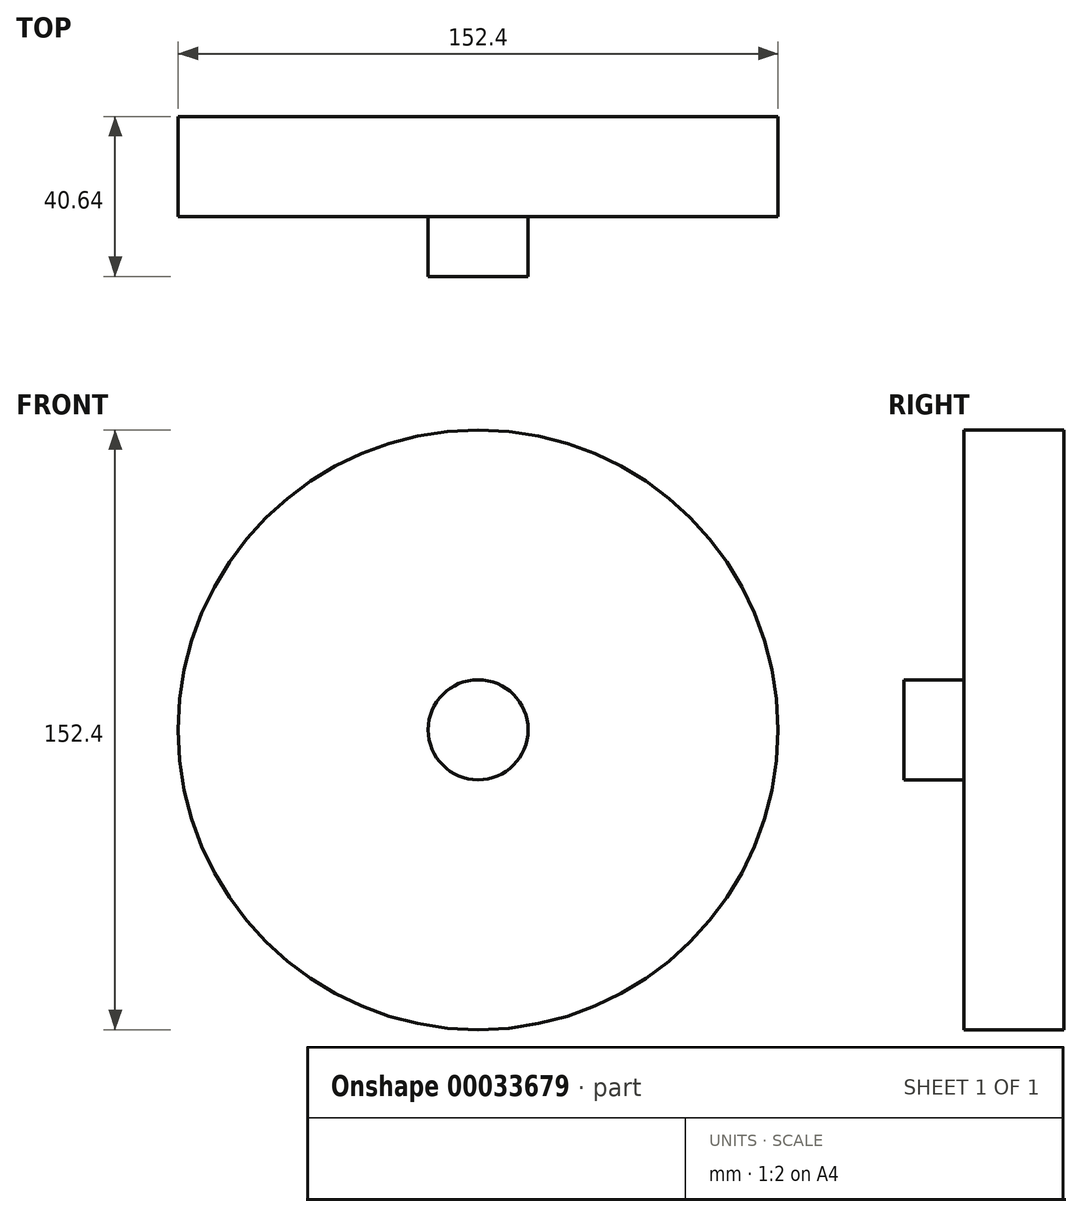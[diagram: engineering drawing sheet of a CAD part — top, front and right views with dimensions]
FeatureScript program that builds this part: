
annotation { "Feature Type Name" : "Feature", "Feature Type Description" : "" }
export const myFeature = defineFeature(function(context is Context, id is Id, definition is map)
    precondition{}
    {
        {
            var Q0;
            Q0=qCreatedBy(makeId("Front.planeOp"),FACE);
            var sketch = newSketch(context, id + "F0", { "sketchPlane" : qUnion([Q0])});
            skCircle(sketch, "E0", {"center": v(0, 0) * mm, "radius": 76.2 * mm});
            skSolve(sketch);
        }
        {
            var Q0;
            Q0=makeQuery(id+"F0.imprint","IMPRINT",FACE,{"disambiguationData":[TD([[makeQuery(id+"F0.imprint","IMPRINT",EDGE,{"derivedFrom":sQuery(id+"F0.wireOp",EDGE,"E0")}),1.0]])]});
            extrude(context, id + "F1", {"entities" : qUnion([Q0]), "depth" : 25.4 * mm});
        }
        {
            var Q0;
            Q0=makeQuery(id+"F1.opExtrude","CAP_FACE",FACE,{"disambiguationData":[OSD([sQuery(id+"F0.wireOp",EDGE,"E0")])],"isStart":false});
            var sketch = newSketch(context, id + "F2", { "sketchPlane" : qUnion([Q0])});
            skCircle(sketch, "E1", {"center": v(0, 0) * mm, "radius": 12.7 * mm});
            skSolve(sketch);
        }
        {
            var Q0;
            Q0 = qSketchRegion(id + "F2", true);
            extrude(context, id + "F3", {"entities" : qUnion([Q0]), "operationType" : NewBodyOperationType.ADD, "depth" : 15.24 * mm});
        }
    });
